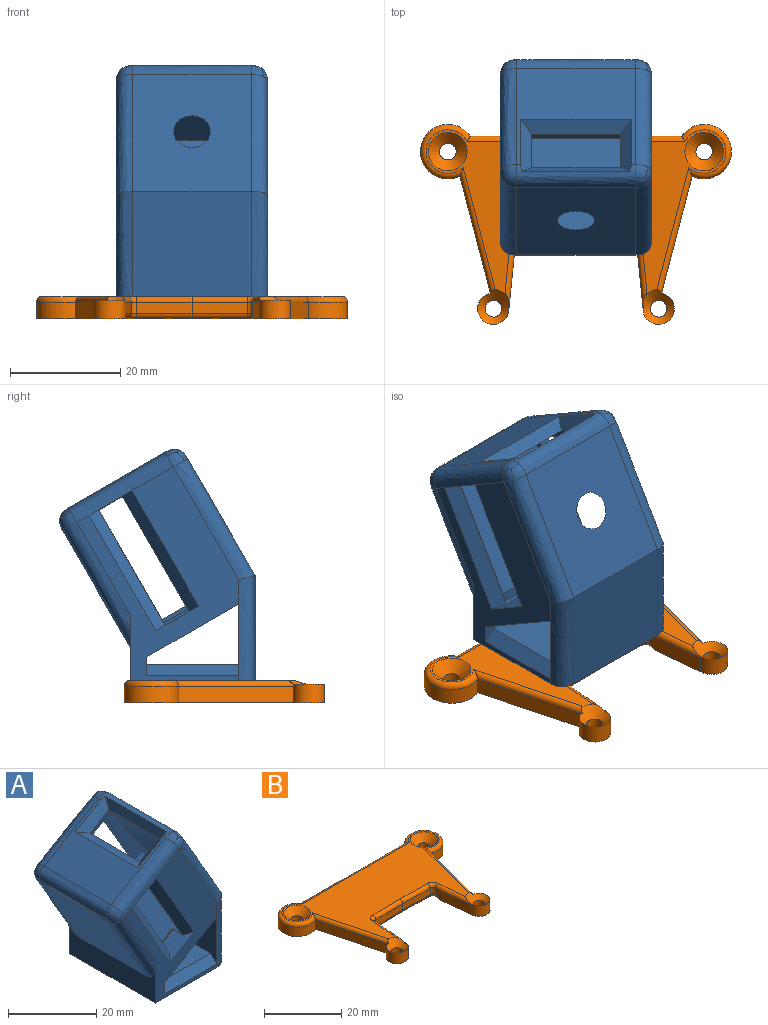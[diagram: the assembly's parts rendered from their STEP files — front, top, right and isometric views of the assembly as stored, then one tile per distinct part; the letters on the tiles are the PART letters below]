
ASSEMBLY  parts=2 mates=1
PART A: 66 faces, bbox 37x30.9x44.5 mm
  f0: plane 8.91x7.39mm, normal (-0.87,0,-0.5), area 23.8mm2, adj f3,f22,f65
  f1: plane 8.91x7.39mm, normal (-0.87,0,-0.5), area 23.8mm2, adj f22,f23,f65
  f2: plane 11.58x7.65mm, normal (-0.87,0,-0.5), area 26.7mm2, adj f19,f23,f65
  f3: plane 26.58x22.34mm, normal (0,1,0), area 287.4mm2, adj f0,f19,f20,f22,f26,f65
  f4: plane 21.5x17.45mm, normal (-0.5,0,0.87), area 242.7mm2, adj f33,f34,f36,f48,f55,f56,f60
  f5: plane 27.5x16.64mm, normal (0.5,0,-0.87), area 528.4mm2, adj f6,f13,f14,f15
  f6: plane 27.5x12.88mm, normal (-1,0,0), area 303.1mm2, adj f5,f7,f29,f30,f50,f53
  f7: plane 23.5x16.64mm, normal (0,0,1), area 391.1mm2, adj f6,f13,f29,f30
  f8: plane 21.5x21.22mm, normal (-0.87,0,-0.5), area 526.7mm2, adj f9,f37,f47,f48,f49
  f9: plane 27.5x12mm, normal (-1,0,0), area 171mm2, adj f8,f10,f14,f15,f47,f49
  f10: plane 27.5x22.64mm, normal (0,0,-1), area 619.6mm2, adj f9,f11,f14,f15,f50,f53
  f11: plane 21.5x19.07mm, normal (1,0,0), area 410.1mm2, adj f10,f12,f50,f53
  f12: plane 21.5x21.22mm, normal (0.87,0,0.5), area 492.1mm2, adj f11,f54,f57,f60,f65
  f13: plane 27.5x3.27mm, normal (1,0,0), area 38.9mm2, adj f5,f7,f14,f15,f29,f30
  f14: plane 38.79x29.29mm, normal (0,-1,0), area 378.2mm2, adj f5,f9,f10,f13,f28,f30,f31,f32
  f15: plane 38.79x29.29mm, normal (0,1,0), area 159mm2, adj f5,f9,f10,f13,f29,f49,f53,f56
  f16: plane 20.05x12.22mm, normal (0,-1,0), area 22.6mm2, adj f18,f19,f36,f37,f38,f48
  f17: plane 20.05x12.22mm, normal (0,1,0), area 22.6mm2, adj f18,f19,f33,f37,f38,f48
  f18: plane 16x0.87mm, normal (-0.87,0,-0.5), area 16mm2, adj f16,f17,f19,f35
  f19: plane 25.33x19.49mm, normal (0.5,0,-0.87), area 207.6mm2, adj f2,f3,f16,f17,f18,f20,f21,f23
  f20: plane 11.58x7.65mm, normal (-0.87,0,-0.5), area 26.7mm2, adj f3,f19,f65
  f21: plane 23.15x20.53mm, normal (0.87,0,0.5), area 548.7mm2, adj f19,f22,f23,f24,f37
  f22: plane 23.76x20.14mm, normal (-0.5,0,0.87), area 506.9mm2, adj f0,f1,f3,f21,f23,f24,f25,f26
  f23: plane 31.78x31.34mm, normal (0,-1,0), area 96.6mm2, adj f1,f2,f19,f21,f22,f61,f62,f63
  f24: plane 23.22x16.51mm, normal (0,1,0), area 127.6mm2, adj f19,f21,f22,f27
  f25: plane 4.58x2.93mm, normal (0,-1,0), area 2.5mm2, adj f22,f26,f27,f28
  f26: plane 20.96x12.1mm, normal (-0.87,0,-0.5), area 5.6mm2, adj f3,f19,f22,f25,f28,f31
  f27: plane 20.96x12.1mm, normal (0.87,0,0.5), area 5.6mm2, adj f19,f22,f24,f25,f28,f32
  f28: plane 7.79x5mm, normal (-0.5,0,0.87), area 29mm2, adj f14,f25,f26,f27,f31,f32
  f29: plane 16.64x2mm, normal (0,0.71,0.71), area 47.1mm2, adj f6,f7,f13,f15
  f30: plane 16.64x2mm, normal (0,-0.71,0.71), area 47.1mm2, adj f6,f7,f13,f14
  f31: plane 21.96x13.83mm, normal (-0.61,-0.71,-0.35), area 68.4mm2, adj f14,f19,f26,f28
  f32: plane 21.96x13.83mm, normal (0.61,-0.71,0.35), area 68.4mm2, adj f14,f19,f27,f28
  f33: plane 9.55x6.07mm, normal (-0.35,0.71,0.61), area 25.3mm2, adj f4,f17,f34,f35,f60
  f34: plane 20x2.73mm, normal (0.26,0,0.97), area 50.9mm2, adj f4,f33,f36,f38
  f35: plane 19.64x2.48mm, normal (-0.97,0,0.26), area 45.8mm2, adj f18,f33,f36,f60
  f36: plane 9.55x6.07mm, normal (-0.35,-0.71,0.61), area 25.3mm2, adj f4,f16,f34,f35,f60
  f37: plane 16x1.83mm, normal (-0.5,0,0.87), area 33.8mm2, adj f8,f16,f17,f21
  f38: plane 16x13.44mm, normal (0.5,0,-0.87), area 248.4mm2, adj f16,f17,f34,f48
  f39: bspline ~3.07x2.56mm, area 5.2mm2, adj f40,f56,f57,f59
  f40: bspline ~2.32x2.25mm, area 5.2mm2, adj f39,f56,f59,f60
  f41: bspline ~3.07x2.56mm, area 5.2mm2, adj f42,f54,f55,f58
  f42: bspline ~2.25x1.95mm, area 5.2mm2, adj f41,f54,f58,f60
  f43: bspline ~2.32x2.25mm, area 5.2mm2, adj f44,f48,f49,f52
  f44: bspline ~2.25x1.95mm, area 5.2mm2, adj f43,f48,f52,f56
  f45: bspline ~2.32x2.25mm, area 5.2mm2, adj f46,f47,f48,f51
  f46: bspline ~3.07x2.56mm, area 5.2mm2, adj f45,f47,f51,f55
  f47: bspline ~22.72x14.85mm, area 110.7mm2, adj f8,f9,f14,f45,f46
  f48: bspline ~30.25x4.1mm, area 88.6mm2, adj f4,f8,f16,f17,f38,f43,f44,f45
  f49: bspline ~22.72x14.85mm, area 110.7mm2, adj f8,f9,f15,f43,f52
  f50: bspline ~20.98x3mm, area 90.9mm2, adj f6,f10,f11,f14,f54
  f51: bspline ~2.25x1.95mm, area 5.2mm2, adj f45,f46,f48,f55
  f52: bspline ~3.07x2.56mm, area 5.2mm2, adj f43,f44,f49,f56
  f53: bspline ~20.98x3mm, area 90.9mm2, adj f6,f10,f11,f15,f57
  f54: bspline ~22.72x14.85mm, area 117.3mm2, adj f12,f14,f41,f42,f50
  f55: bspline ~18.95x12.67mm, area 98.1mm2, adj f4,f14,f19,f41,f46,f51,f58
  f56: bspline ~18.95x12.67mm, area 98.1mm2, adj f4,f15,f39,f40,f44,f52
  f57: bspline ~22.72x14.85mm, area 117.3mm2, adj f12,f15,f39,f53,f59
  f58: bspline ~2.32x2.25mm, area 5.2mm2, adj f41,f42,f55,f60
  f59: bspline ~2.25x1.95mm, area 5.2mm2, adj f39,f40,f57,f60
  f60: bspline ~30.25x4.1mm, area 78.6mm2, adj f4,f12,f33,f35,f36,f40,f42,f58
  f61: plane 19.87x11.58mm, normal (0.86,0,0.5), area 50mm2, adj f15,f23,f62,f64
  f62: plane 16.42x9.57mm, normal (0.5,0,-0.86), area 41.3mm2, adj f15,f23,f61,f63
  f63: plane 19.87x11.58mm, normal (-0.86,0,-0.5), area 50mm2, adj f15,f23,f62,f64
  f64: plane 16.42x9.57mm, normal (-0.5,0,0.86), area 41.3mm2, adj f15,f23,f61,f63
  f65: cone r=12mm half-angle=80deg, axis (-0.87,0,-0.5), area 420.5mm2, adj f0,f1,f2,f3,f12,f20,f22,f23
PART B: 39 faces, bbox 57.2x37.4x4 mm
  f0: cylinder r=4.95mm len=9.9mm, axis (0,0,-1), area 67.7mm2, adj f1,f16,f18,f35
  f1: plane 21.26x5.56mm, normal (-0.97,-0.25,0), area 65.9mm2, adj f0,f2,f18,f34
  f2: cylinder r=2.84mm len=5.68mm, axis (0,0,-1), area 43.9mm2, adj f1,f3,f18,f20,f23,f28,f34
  f3: plane 12.01x2mm, normal (1,-0.1,0), area 24.1mm2, adj f2,f4,f23,f28
  f4: cylinder r=1mm len=2mm, axis (0,0,-1), area 2.9mm2, adj f3,f5,f24,f30
  f5: plane 9.99x2mm, normal (0.01,-1,0), area 20mm2, adj f4,f6,f25,f32
  f6: plane 9.99x2mm, normal (-0.01,-1,0), area 20mm2, adj f5,f7,f26,f33
  f7: cylinder r=1mm len=2mm, axis (0,0,-1), area 2.9mm2, adj f6,f8,f27,f31
  f8: plane 12.01x3mm, normal (-1,-0.1,0), area 35.6mm2, adj f7,f9,f18,f27,f29
  f9: cylinder r=2.84mm len=5.68mm, axis (0,0,-1), area 43.1mm2, adj f8,f10,f18,f19,f29,f37
  f10: plane 21.26x5.56mm, normal (0.97,-0.25,0), area 65.9mm2, adj f9,f11,f18,f37
  f11: cylinder r=4.95mm len=9.9mm, axis (0,0,-1), area 67.7mm2, adj f10,f16,f18,f38
  f12: cylinder r=1.5mm len=3mm, axis (0,0,-1), area 18.8mm2, adj f18,f22
  f13: cylinder r=1.5mm len=3mm, axis (0,0,-1), area 18.8mm2, adj f18,f20
  f14: cylinder r=1.5mm len=3mm, axis (0,0,-1), area 18.8mm2, adj f18,f19
  f15: cylinder r=1.5mm len=3mm, axis (0,0,-1), area 18.8mm2, adj f18,f21
  f16: plane 38.39x3mm, normal (0,1,0), area 115.2mm2, adj f0,f11,f18,f36
  f17: plane 54.4x29.66mm, normal (0,0,1), area 726.8mm2, adj f19,f20,f21,f22,f28,f29,f30,f31
  f18: plane 56.4x36.29mm, normal (0,0,-1), area 965mm2, adj f0,f1,f2,f8,f9,f10,f11,f12
  f19: cone r=3.5mm half-angle=45deg, axis (0,0,1), area 29.2mm2, adj f9,f14,f17,f29,f37
  f20: cone r=1.5mm half-angle=45deg, axis (0,0,1), area 29.2mm2, adj f2,f13,f17,f28,f34
  f21: cone r=3.5mm half-angle=45deg, axis (0,0,1), area 44.4mm2, adj f15,f17
  f22: cone r=1.5mm half-angle=45deg, axis (0,0,1), area 44.4mm2, adj f12,f17
  f23: cylinder r=1mm len=12.11mm, axis (0.1,1,0), area 17.4mm2, adj f2,f3,f18,f24
  f24: torus R=2mm, axis (0,0,1), area 3.1mm2, adj f4,f18,f23,f25
  f25: cylinder r=1mm len=10.01mm, axis (1,0.01,0), area 15.7mm2, adj f5,f18,f24,f26
  f26: cylinder r=1mm len=10.01mm, axis (1,-0.01,0), area 15.7mm2, adj f6,f18,f25,f27
  f27: torus R=2mm, axis (0,0,1), area 4.6mm2, adj f7,f8,f18,f26
  f28: cylinder r=1mm len=12.11mm, axis (-0.1,-1,0), area 16.6mm2, adj f2,f3,f17,f20,f30
  f29: cylinder r=1mm len=12.11mm, axis (-0.1,1,0), area 16.6mm2, adj f8,f9,f17,f19,f31
  f30: torus R=2mm, axis (0,0,1), area 3.1mm2, adj f4,f17,f28,f32
  f31: torus R=2mm, axis (0,0,1), area 3.1mm2, adj f7,f17,f29,f33
  f32: cylinder r=1mm len=10.01mm, axis (-1,-0.01,0), area 15.7mm2, adj f5,f17,f30,f33
  f33: cylinder r=1mm len=10.01mm, axis (-1,0.01,0), area 15.7mm2, adj f6,f17,f31,f32
  f34: cylinder r=1mm len=22.91mm, axis (-0.25,0.97,0), area 34.9mm2, adj f1,f2,f17,f20,f35
  f35: torus R=3.95mm, axis (0,0,1), area 33.9mm2, adj f0,f17,f34,f36
  f36: cylinder r=1mm len=39.51mm, axis (1,0,0), area 60.9mm2, adj f16,f17,f35,f38
  f37: cylinder r=1mm len=22.91mm, axis (-0.25,-0.97,0), area 34.9mm2, adj f9,f10,f17,f19,f38
  f38: torus R=3.95mm, axis (0,0,1), area 33.9mm2, adj f11,f17,f36,f37
PLACE A rot(axis=(0,0,-1),90deg) t=(20.68,26.71,41.13)mm
PLACE B t=(20.68,23.7,17.33)mm
MATE fastened A.f10 <-> B.f17  axis (0,0,-1) through (20.68,29.89,21.33)mm
